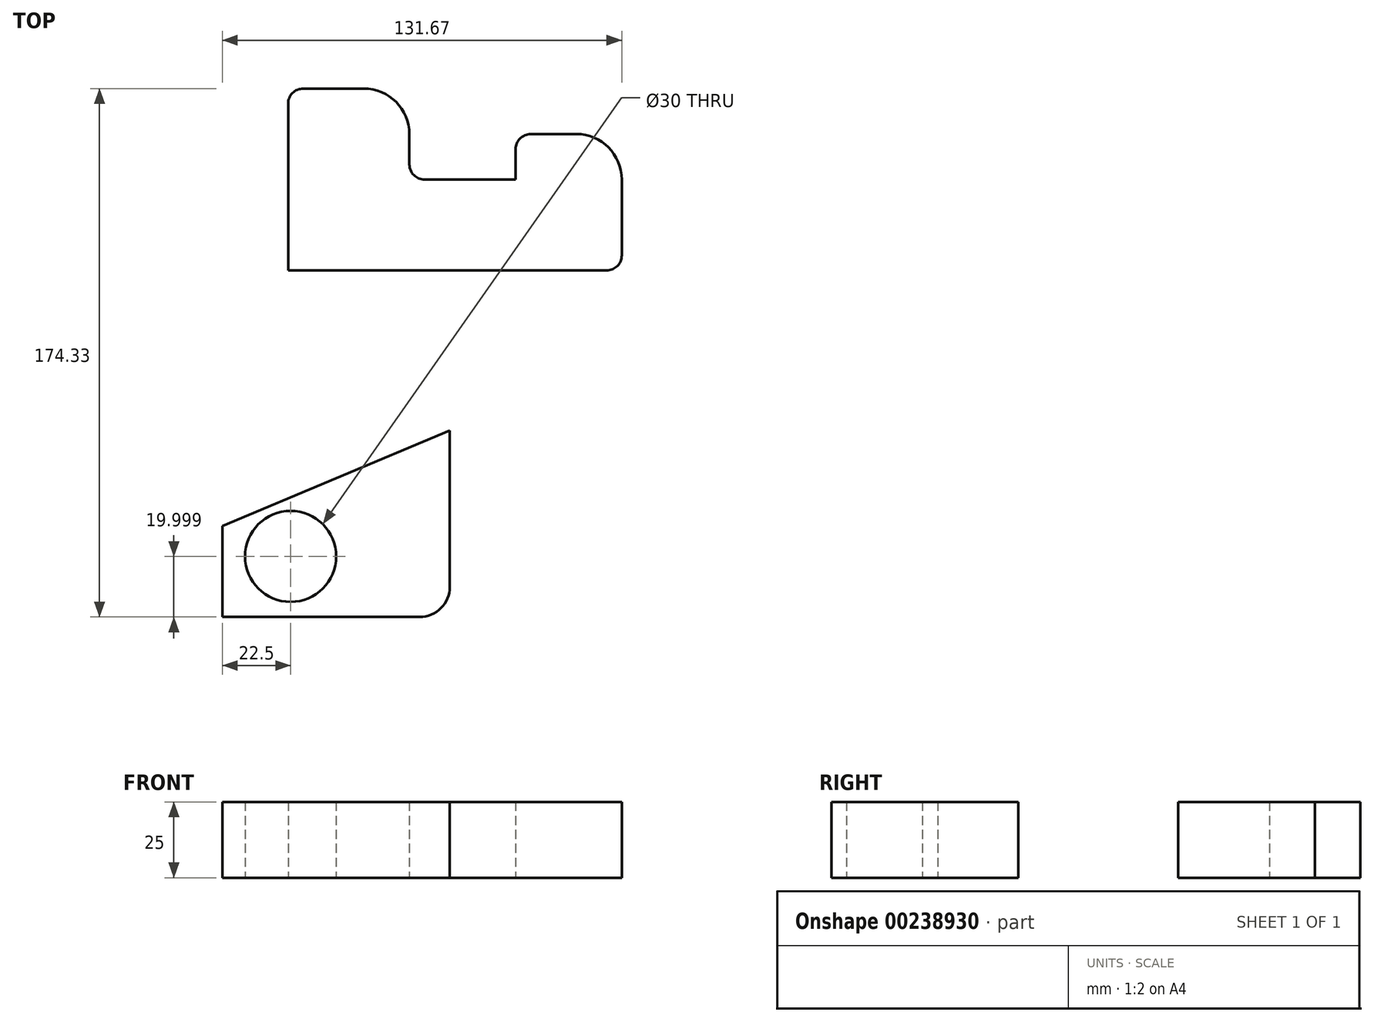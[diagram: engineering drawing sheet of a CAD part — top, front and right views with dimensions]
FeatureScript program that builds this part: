
annotation { "Feature Type Name" : "Feature", "Feature Type Description" : "" }
export const myFeature = defineFeature(function(context is Context, id is Id, definition is map)
    precondition{}
    {
        {
            var Q0;
            Q0=qCreatedBy(makeId("Top.planeOp"),FACE);
            var sketch = newSketch(context, id + "F0", { "sketchPlane" : qUnion([Q0])});
            skLineSegment(sketch, "E0", {"start": v(-79.16, -22.66) * mm, "end": v(25.84, -22.66) * mm});
            skLineSegment(sketch, "E1", {"start": v(-79.16, -22.66) * mm, "end": v(-79.16, 32.34) * mm});
            skLineSegment(sketch, "E2", {"start": v(-74.16, 37.34) * mm, "end": v(-54.16, 37.34) * mm});
            skLineSegment(sketch, "E3", {"start": v(-39.16, 22.34) * mm, "end": v(-39.16, 12.34) * mm});
            skLineSegment(sketch, "E4", {"start": v(-34.16, 7.34) * mm, "end": v(-4.16, 7.34) * mm});
            skLineSegment(sketch, "E5", {"start": v(-4.16, 7.34) * mm, "end": v(-4.16, 17.34) * mm});
            skLineSegment(sketch, "E6", {"start": v(0.84, 22.34) * mm, "end": v(15.84, 22.34) * mm});
            skLineSegment(sketch, "E7", {"start": v(30.84, 7.34) * mm, "end": v(30.84, -17.66) * mm});
            skPoint(sketch, "E8.visualSharp", {"position": v(-79.16, 37.34) * mm});
            skArc(sketch, "E8.filletArc", {"start": v(-74.16, 37.34) * mm, "mid": v(-77.7, 35.88) * mm, "end": v(-79.16, 32.34) * mm});
            skPoint(sketch, "E9.visualSharp", {"position": v(30.84, -22.66) * mm});
            skArc(sketch, "E9.filletArc", {"start": v(25.84, -22.66) * mm, "mid": v(29.38, -21.2) * mm, "end": v(30.84, -17.66) * mm});
            skPoint(sketch, "E10.visualSharp", {"position": v(30.84, 22.34) * mm});
            skArc(sketch, "E10.filletArc", {"start": v(30.84, 7.34) * mm, "mid": v(26.45, 17.95) * mm, "end": v(15.84, 22.34) * mm});
            skPoint(sketch, "E11.visualSharp", {"position": v(-4.16, 22.34) * mm});
            skArc(sketch, "E11.filletArc", {"start": v(0.84, 22.34) * mm, "mid": v(-2.7, 20.88) * mm, "end": v(-4.16, 17.34) * mm});
            skPoint(sketch, "E12.visualSharp", {"position": v(-39.16, 7.34) * mm});
            skArc(sketch, "E12.filletArc", {"start": v(-39.16, 12.34) * mm, "mid": v(-37.7, 8.8) * mm, "end": v(-34.16, 7.34) * mm});
            skPoint(sketch, "E13.visualSharp", {"position": v(-39.16, 37.34) * mm});
            skArc(sketch, "E13.filletArc", {"start": v(-39.16, 22.34) * mm, "mid": v(-43.55, 32.95) * mm, "end": v(-54.16, 37.34) * mm});
            skLineSegment(sketch, "E14", {"start": v(-100.83, -137) * mm, "end": v(-35.83, -137) * mm});
            skLineSegment(sketch, "E15", {"start": v(-100.83, -137) * mm, "end": v(-100.83, -107) * mm});
            skLineSegment(sketch, "E16", {"start": v(-25.83, -127) * mm, "end": v(-25.83, -75.47) * mm});
            skLineSegment(sketch, "E17", {"start": v(-25.83, -75.47) * mm, "end": v(-100.83, -107) * mm});
            skPoint(sketch, "E18.visualSharp", {"position": v(-25.83, -137) * mm});
            skArc(sketch, "E18.filletArc", {"start": v(-35.83, -137) * mm, "mid": v(-28.76, -134.06) * mm, "end": v(-25.83, -127) * mm});
            skLineSegment(sketch, "E19", {"start": v(-100.83, -137) * mm, "end": v(-78.33, -137) * mm});
            skLineSegment(sketch, "E20", {"start": v(-100.83, -137) * mm, "end": v(-100.83, -117) * mm});
            skLineSegment(sketch, "E21", {"start": v(-78.33, -137) * mm, "end": v(-78.33, -117) * mm, "construction": true});
            skLineSegment(sketch, "E22", {"start": v(-78.33, -117) * mm, "end": v(-100.83, -117) * mm, "construction": true});
            skCircle(sketch, "E23", {"center": v(-78.33, -117) * mm, "radius": 15 * mm});
            skSolve(sketch);
        }
        {
            var Q0;
            Q0=makeQuery(id+"F0.imprint","IMPRINT",FACE,{"disambiguationData":[TD([[makeQuery(id+"F0.imprint","IMPRINT",EDGE,{"derivedFrom":sQuery(id+"F0.wireOp",EDGE,"E0")}),1.0]])]});
            extrude(context, id + "F1", {"entities" : qUnion([Q0]), "depth" : 25 * mm});
        }
        {
            var Q0;
            Q0=makeQuery(id+"F0.imprint","IMPRINT",FACE,{"disambiguationData":[TD([[makeQuery(id+"F0.imprint","IMPRINT",EDGE,{"derivedFrom":sQuery(id+"F0.wireOp",EDGE,"E14")}),1.0]])]});
            extrude(context, id + "F2", {"entities" : qUnion([Q0]), "depth" : 25 * mm});
        }
    });
